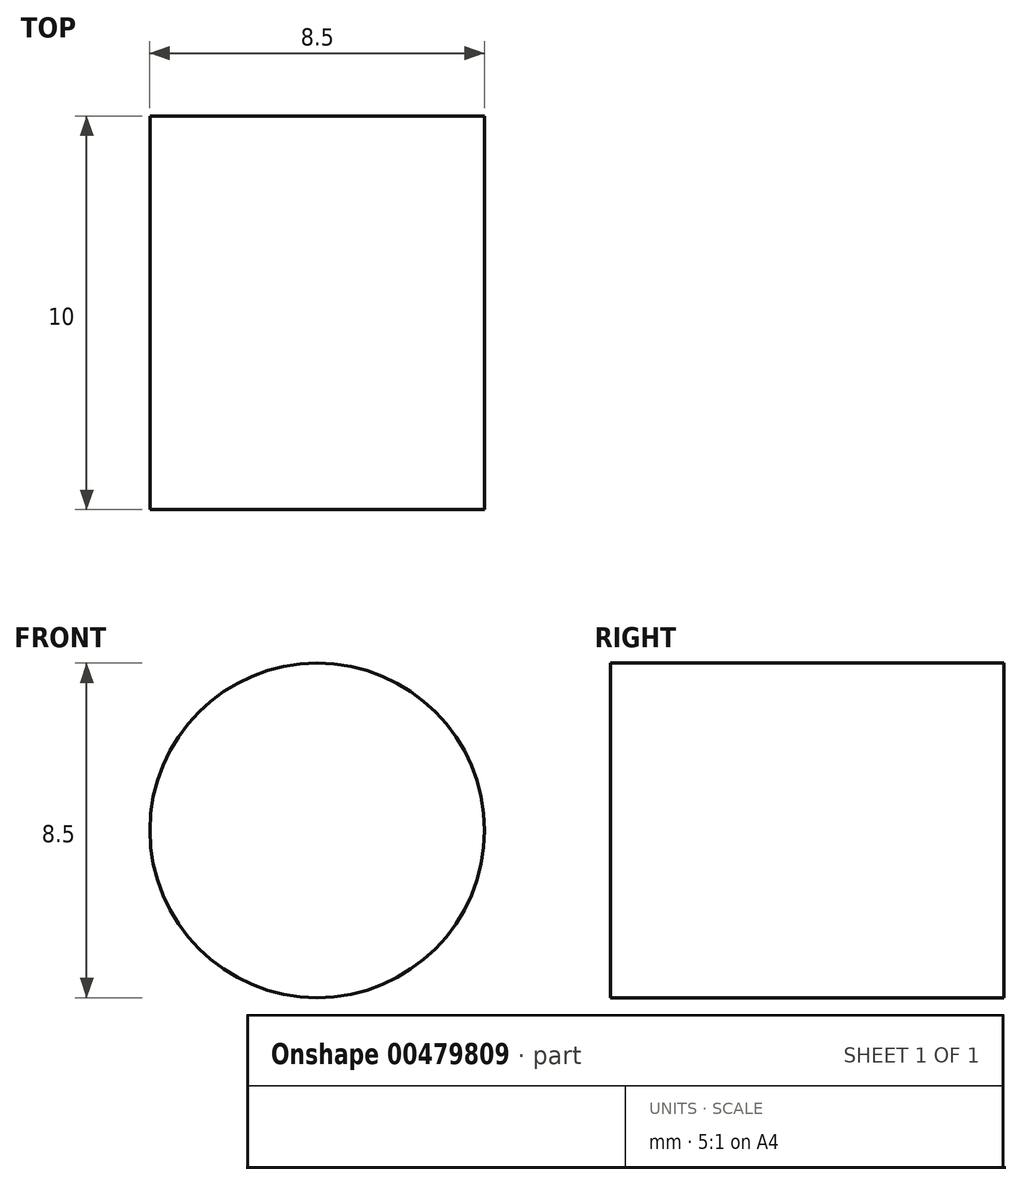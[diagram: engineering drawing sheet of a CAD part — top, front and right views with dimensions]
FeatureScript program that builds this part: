
annotation { "Feature Type Name" : "Feature", "Feature Type Description" : "" }
export const myFeature = defineFeature(function(context is Context, id is Id, definition is map)
    precondition{}
    {
        {
            var Q0;
            Q0=qCreatedBy(makeId("Front.planeOp"),FACE);
            var sketch = newSketch(context, id + "F0", { "sketchPlane" : qUnion([Q0])});
            skCircle(sketch, "E0", {"center": v(-108.07, 3.02) * mm, "radius": 4.25 * mm});
            skSolve(sketch);
        }
        {
            var Q0;
            Q0=makeQuery(id+"F0.imprint","IMPRINT",FACE,{"disambiguationData":[TD([[makeQuery(id+"F0.imprint","IMPRINT",EDGE,{"derivedFrom":sQuery(id+"F0.wireOp",EDGE,"E0")}),1.0]])]});
            extrude(context, id + "F1", {"entities" : qUnion([Q0]), "depth" : 10 * mm});
        }
    });
